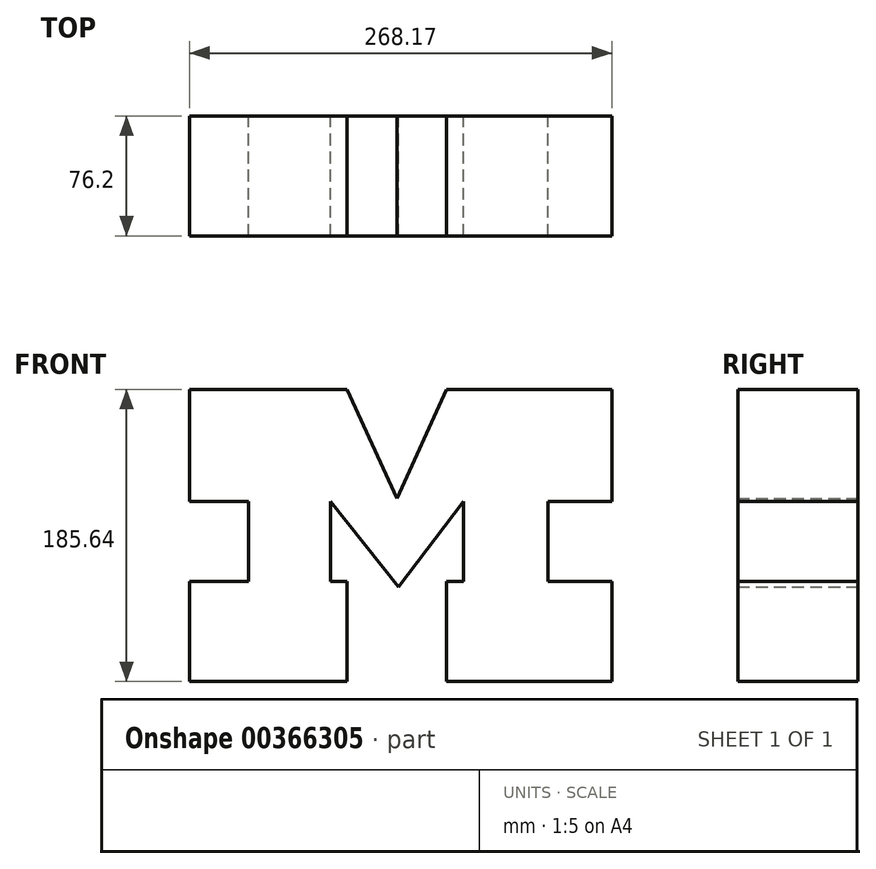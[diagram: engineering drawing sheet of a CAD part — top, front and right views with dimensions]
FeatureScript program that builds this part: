
annotation { "Feature Type Name" : "Feature", "Feature Type Description" : "" }
export const myFeature = defineFeature(function(context is Context, id is Id, definition is map)
    precondition{}
    {
        {
            var Q0;
            Q0=qCreatedBy(makeId("Front.planeOp"),FACE);
            var sketch = newSketch(context, id + "F0", { "sketchPlane" : qUnion([Q0])});
            skLineSegment(sketch, "E0", {"start": v(26.16, 79.76) * mm, "end": v(126.05, 79.76) * mm});
            skLineSegment(sketch, "E1", {"start": v(126.05, 79.76) * mm, "end": v(157.74, 10.46) * mm});
            skLineSegment(sketch, "E2", {"start": v(157.74, 10.46) * mm, "end": v(189.42, 79.76) * mm});
            skLineSegment(sketch, "E3", {"start": v(189.42, 79.76) * mm, "end": v(294.33, 79.76) * mm});
            skLineSegment(sketch, "E4", {"start": v(294.33, 8.42) * mm, "end": v(253.87, 8.42) * mm});
            skLineSegment(sketch, "E5", {"start": v(253.87, 8.42) * mm, "end": v(253.87, -42.38) * mm});
            skLineSegment(sketch, "E6", {"start": v(253.87, -42.38) * mm, "end": v(294.33, -42.38) * mm});
            skLineSegment(sketch, "E7", {"start": v(294.33, -105.88) * mm, "end": v(189.42, -105.88) * mm});
            skLineSegment(sketch, "E8", {"start": v(189.42, -105.88) * mm, "end": v(189.42, -42.38) * mm});
            skLineSegment(sketch, "E9", {"start": v(189.42, -42.38) * mm, "end": v(199.98, -42.38) * mm});
            skLineSegment(sketch, "E10", {"start": v(199.98, -42.38) * mm, "end": v(199.98, 8.42) * mm});
            skLineSegment(sketch, "E11", {"start": v(115.49, 8.42) * mm, "end": v(115.49, -42.38) * mm});
            skLineSegment(sketch, "E12", {"start": v(115.49, -42.38) * mm, "end": v(126.05, -42.38) * mm});
            skLineSegment(sketch, "E13", {"start": v(126.05, -42.38) * mm, "end": v(126.05, -105.88) * mm});
            skLineSegment(sketch, "E14", {"start": v(126.05, -105.88) * mm, "end": v(26.16, -105.88) * mm});
            skLineSegment(sketch, "E15", {"start": v(0, -105.88) * mm, "end": v(0, -42.38) * mm});
            skLineSegment(sketch, "E16", {"start": v(26.16, -42.38) * mm, "end": v(63.5, -42.38) * mm});
            skLineSegment(sketch, "E17", {"start": v(63.5, -42.38) * mm, "end": v(63.5, 8.42) * mm});
            skLineSegment(sketch, "E18", {"start": v(63.5, 8.42) * mm, "end": v(26.16, 8.42) * mm});
            skLineSegment(sketch, "E19", {"start": v(294.33, -42.38) * mm, "end": v(294.33, -105.88) * mm});
            skLineSegment(sketch, "E20", {"start": v(294.33, -105.88) * mm, "end": v(294.33, -42.38) * mm});
            skLineSegment(sketch, "E21", {"start": v(26.16, 79.76) * mm, "end": v(26.16, 8.42) * mm});
            skLineSegment(sketch, "E22.trimOffspring", {"start": v(26.16, -42.38) * mm, "end": v(26.16, -105.88) * mm});
            skPoint(sketch, "E23.orphan", {"position": v(0, 79.76) * mm});
            skPoint(sketch, "E24.orphan", {"position": v(0, 8.42) * mm});
            skPoint(sketch, "E25.start.orphan", {"position": v(317.37, -42.38) * mm});
            skPoint(sketch, "E26.orphan", {"position": v(317.37, -105.88) * mm});
            skLineSegment(sketch, "E27.trimOffspring", {"start": v(294.33, 8.42) * mm, "end": v(294.33, 79.76) * mm});
            skPoint(sketch, "E28.orphan", {"position": v(317.37, 79.76) * mm});
            skPoint(sketch, "E29.orphan", {"position": v(317.37, 8.42) * mm});
            skLineSegment(sketch, "E30", {"start": v(115.49, 8.42) * mm, "end": v(158.74, -45.79) * mm});
            skLineSegment(sketch, "E31", {"start": v(158.74, -45.79) * mm, "end": v(199.98, 8.42) * mm});
            skSolve(sketch);
        }
        {
            var Q0;
            Q0=makeQuery(id+"F0.imprint","IMPRINT",FACE,{"disambiguationData":[TD([[makeQuery(id+"F0.imprint","IMPRINT",EDGE,{"derivedFrom":sQuery(id+"F0.wireOp",EDGE,"E0")}),-1.0]])]});
            extrude(context, id + "F1", {"entities" : qUnion([Q0]), "depth" : 76.2 * mm});
        }
    });
